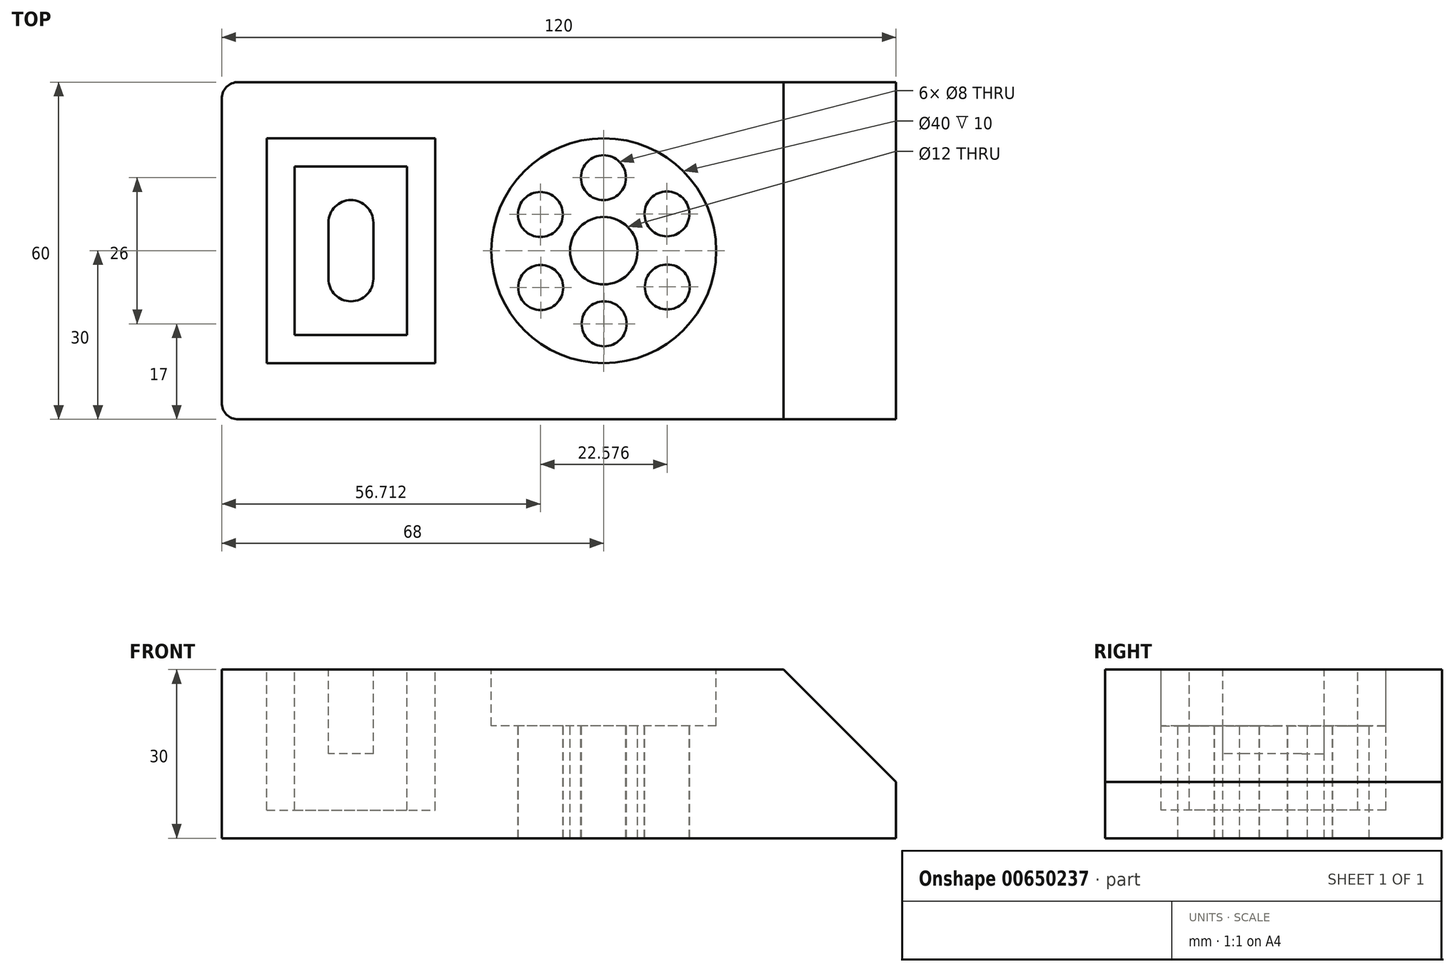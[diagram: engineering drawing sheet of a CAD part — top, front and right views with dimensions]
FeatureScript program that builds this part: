
annotation { "Feature Type Name" : "Feature", "Feature Type Description" : "" }
export const myFeature = defineFeature(function(context is Context, id is Id, definition is map)
    precondition{}
    {
        {
            var Q0;
            Q0=qCreatedBy(makeId("Front.planeOp"),FACE);
            var sketch = newSketch(context, id + "F0", { "sketchPlane" : qUnion([Q0])});
            skLineSegment(sketch, "E0", {"start": v(0, 0) * mm, "end": v(0, 50) * mm});
            skLineSegment(sketch, "E1", {"start": v(0, 50) * mm, "end": v(-120, 50) * mm});
            skLineSegment(sketch, "E2", {"start": v(-120, 50) * mm, "end": v(-120, 0) * mm});
            skLineSegment(sketch, "E3", {"start": v(-120, 0) * mm, "end": v(0, 0) * mm});
            skSolve(sketch);
        }
        {
            var Q0;
            Q0=makeQuery(id+"F0.imprint","IMPRINT",FACE,{"disambiguationData":[TD([[makeQuery(id+"F0.imprint","IMPRINT",EDGE,{"derivedFrom":sQuery(id+"F0.wireOp",EDGE,"E0")}),1.0]])]});
            extrude(context, id + "F1", {"entities" : qUnion([Q0]), "depth" : 60 * mm, "offsetDistance" : 25 * mm});
        }
        {
            var Q0;
            Q0=makeQuery(id+"F1.opExtrude","SWEPT_FACE",FACE,{"disambiguationData":[OSD([sQuery(id+"F0.wireOp",EDGE,"E1")])]});
            var sketch = newSketch(context, id + "F2", { "sketchPlane" : qUnion([Q0])});
            skLineSegment(sketch, "E4.bottom", {"start": v(-112, -10) * mm, "end": v(-82, -10) * mm});
            skLineSegment(sketch, "E4.top", {"start": v(-112, -50) * mm, "end": v(-82, -50) * mm});
            skLineSegment(sketch, "E4.left", {"start": v(-112, -10) * mm, "end": v(-112, -50) * mm});
            skLineSegment(sketch, "E4.right", {"start": v(-82, -10) * mm, "end": v(-82, -50) * mm});
            skLineSegment(sketch, "E5.bottom", {"start": v(-107, -15) * mm, "end": v(-87, -15) * mm});
            skLineSegment(sketch, "E5.top", {"start": v(-107, -45) * mm, "end": v(-87, -45) * mm});
            skLineSegment(sketch, "E5.left", {"start": v(-107, -15) * mm, "end": v(-107, -45) * mm});
            skLineSegment(sketch, "E5.right", {"start": v(-87, -15) * mm, "end": v(-87, -45) * mm});
            skSolve(sketch);
        }
        {
            var Q0;
            Q0=makeQuery(id+"F2.imprint","IMPRINT",FACE,{"disambiguationData":[TD([[makeQuery(id+"F2.imprint","IMPRINT",EDGE,{"derivedFrom":sQuery(id+"F2.wireOp",EDGE,"E4.bottom")}),-1.0]])]});
            extrude(context, id + "F3", {"entities" : qUnion([Q0]), "operationType" : NewBodyOperationType.REMOVE, "oppositeDirection" : true, "depth" : 25 * mm, "offsetDistance" : 25 * mm});
        }
        {
            var Q0;
            Q0=makeQuery(id+"F3.boolean.opBoolean","SPLIT",FACE,{"disambiguationData":[TD([makeQuery(id+"F3.opExtrude","SWEPT_FACE",FACE,{"disambiguationData":[OSD([sQuery(id+"F2.wireOp",EDGE,"E5.bottom")])]})])],"derivedFrom":makeQuery(id+"F1.opExtrude","SWEPT_FACE",FACE,{"disambiguationData":[OSD([sQuery(id+"F0.wireOp",EDGE,"E1")])]})});
            var sketch = newSketch(context, id + "F4", { "sketchPlane" : qUnion([Q0])});
            skLineSegment(sketch, "E6.bottom", {"start": v(-97, -21) * mm, "end": v(-97, -21) * mm});
            skLineSegment(sketch, "E6.top", {"start": v(-97, -39) * mm, "end": v(-97, -39) * mm});
            skLineSegment(sketch, "E6.left", {"start": v(-101, -25) * mm, "end": v(-101, -35) * mm});
            skLineSegment(sketch, "E6.right", {"start": v(-93, -25) * mm, "end": v(-93, -35) * mm});
            skPoint(sketch, "E7.visualSharp", {"position": v(-101, -21) * mm});
            skArc(sketch, "E7.filletArc", {"start": v(-97, -21) * mm, "mid": v(-99.83, -22.17) * mm, "end": v(-101, -25) * mm});
            skPoint(sketch, "E8.visualSharp", {"position": v(-93, -21) * mm});
            skArc(sketch, "E8.filletArc", {"start": v(-93, -25) * mm, "mid": v(-94.17, -22.17) * mm, "end": v(-97, -21) * mm});
            skPoint(sketch, "E9.visualSharp", {"position": v(-101, -39) * mm});
            skArc(sketch, "E9.filletArc", {"start": v(-101, -35) * mm, "mid": v(-99.83, -37.83) * mm, "end": v(-97, -39) * mm});
            skPoint(sketch, "E10.visualSharp", {"position": v(-93, -39) * mm});
            skArc(sketch, "E10.filletArc", {"start": v(-97, -39) * mm, "mid": v(-94.17, -37.83) * mm, "end": v(-93, -35) * mm});
            skSolve(sketch);
        }
        {
            var Q0;
            Q0=makeQuery(id+"F4.imprint","IMPRINT",FACE,{"disambiguationData":[TD([[makeQuery(id+"F4.imprint","IMPRINT",EDGE,{"derivedFrom":sQuery(id+"F4.wireOp",EDGE,"E6.left")}),1.0]])]});
            extrude(context, id + "F5", {"entities" : qUnion([Q0]), "operationType" : NewBodyOperationType.REMOVE, "oppositeDirection" : true, "depth" : 15 * mm, "offsetDistance" : 25 * mm});
        }
        {
            var Q0;
            Q0=makeQuery(id+"F1.opExtrude","SWEPT_FACE",FACE,{"disambiguationData":[OSD([sQuery(id+"F0.wireOp",EDGE,"E3")])]});
            var sketch = newSketch(context, id + "F6", { "sketchPlane" : qUnion([Q0])});
            skLineSegment(sketch, "E11.bottom", {"start": v(-120, 60) * mm, "end": v(0, 60) * mm});
            skLineSegment(sketch, "E11.top", {"start": v(-120, 0) * mm, "end": v(0, 0) * mm});
            skLineSegment(sketch, "E11.left", {"start": v(-120, 60) * mm, "end": v(-120, 0) * mm});
            skLineSegment(sketch, "E11.right", {"start": v(0, 60) * mm, "end": v(0, 0) * mm});
            skSolve(sketch);
        }
        {
            var Q0;
            Q0=makeQuery(id+"F1.opExtrude","SWEPT_EDGE",EDGE,{"disambiguationData":[OSD([sQuery(id+"F0.wireOp",EDGE,"E0"),sQuery(id+"F0.wireOp",EDGE,"E1")])]});
            chamfer(context, id + "F7", {"entities" : qUnion([Q0]), "width" : 20 * mm, "tangentPropagation" : true});
        }
        {
            var Q0;
            {var subQ2=sQuery(id+"F0.wireOp",EDGE,"E1");var subQ3=sQuery(id+"F0.wireOp",EDGE,"E0");Q0=makeQuery(id+"F3.boolean.opBoolean","SPLIT",FACE,{"disambiguationData":[TD([makeQuery(id+"F1.opExtrude","SWEPT_FACE",FACE,{"disambiguationData":[OSD([subQ3])]})])],"derivedFrom":makeQuery(id+"F1.opExtrude","SWEPT_FACE",FACE,{"disambiguationData":[OSD([subQ2])]})});}
            var sketch = newSketch(context, id + "F8", { "sketchPlane" : qUnion([Q0])});
            skCircle(sketch, "E12", {"center": v(-52, -30) * mm, "radius": 20 * mm});
            skPoint(sketch, "E12.centerSnap0", {"position": v(-82, -30) * mm});
            skSolve(sketch);
        }
        {
            var Q0;
            Q0=makeQuery(id+"F8.imprint","IMPRINT",FACE,{"disambiguationData":[TD([[makeQuery(id+"F8.imprint","IMPRINT",EDGE,{"derivedFrom":sQuery(id+"F8.wireOp",EDGE,"E12")}),1.0]])]});
            extrude(context, id + "F9", {"entities" : qUnion([Q0]), "operationType" : NewBodyOperationType.REMOVE, "oppositeDirection" : true, "depth" : 10 * mm, "offsetDistance" : 25 * mm});
        }
        {
            var Q0;
            Q0=makeQuery(id+"F9.boolean.opBoolean","COPY",FACE,{"derivedFrom":makeQuery(id+"F9.opExtrude","CAP_FACE",FACE,{"disambiguationData":[OSD([sQuery(id+"F8.wireOp",EDGE,"E12")])],"isStart":false})});
            var sketch = newSketch(context, id + "F10", { "sketchPlane" : qUnion([Q0])});
            skCircle(sketch, "E13", {"center": v(-63.23, -36.55) * mm, "radius": 4 * mm});
            skCircle(sketch, "E14.1.0", {"center": v(-63.29, -23.55) * mm, "radius": 4 * mm});
            skCircle(sketch, "E14.2.0", {"center": v(-52.06, -17) * mm, "radius": 4 * mm});
            skCircle(sketch, "E14.3.0", {"center": v(-40.77, -23.45) * mm, "radius": 4 * mm});
            skCircle(sketch, "E14.4.0", {"center": v(-40.71, -36.45) * mm, "radius": 4 * mm});
            skCircle(sketch, "E14.5.0", {"center": v(-51.94, -43) * mm, "radius": 4 * mm});
            skPoint(sketch, "E14.center", {"position": v(-52, -30) * mm});
            skLineSegment(sketch, "E14.anchor1", {"start": v(-52, -30) * mm, "end": v(-63.23, -36.55) * mm, "construction": true});
            skLineSegment(sketch, "E14.anchor2", {"start": v(-52, -30) * mm, "end": v(-51.94, -43) * mm, "construction": true});
            skSolve(sketch);
        }
        {
            var Q0;
            Q0=makeQuery(id+"F10.imprint","IMPRINT",FACE,{"disambiguationData":[TD([[makeQuery(id+"F10.imprint","IMPRINT",EDGE,{"derivedFrom":sQuery(id+"F10.wireOp",EDGE,"E14.2.0")}),1.0]])]});
            var Q1;
            Q1=makeQuery(id+"F10.imprint","IMPRINT",FACE,{"disambiguationData":[TD([[makeQuery(id+"F10.imprint","IMPRINT",EDGE,{"derivedFrom":sQuery(id+"F10.wireOp",EDGE,"E14.1.0")}),1.0]])]});
            var Q2;
            Q2=makeQuery(id+"F10.imprint","IMPRINT",FACE,{"disambiguationData":[TD([[makeQuery(id+"F10.imprint","IMPRINT",EDGE,{"derivedFrom":sQuery(id+"F10.wireOp",EDGE,"E13")}),1.0]])]});
            var Q3;
            Q3=makeQuery(id+"F10.imprint","IMPRINT",FACE,{"disambiguationData":[TD([[makeQuery(id+"F10.imprint","IMPRINT",EDGE,{"derivedFrom":sQuery(id+"F10.wireOp",EDGE,"E14.5.0")}),1.0]])]});
            var Q4;
            Q4=makeQuery(id+"F10.imprint","IMPRINT",FACE,{"disambiguationData":[TD([[makeQuery(id+"F10.imprint","IMPRINT",EDGE,{"derivedFrom":sQuery(id+"F10.wireOp",EDGE,"E14.4.0")}),1.0]])]});
            var Q5;
            Q5=makeQuery(id+"F10.imprint","IMPRINT",FACE,{"disambiguationData":[TD([[makeQuery(id+"F10.imprint","IMPRINT",EDGE,{"derivedFrom":sQuery(id+"F10.wireOp",EDGE,"E14.3.0")}),1.0]])]});
            extrude(context, id + "F11", {"entities" : qUnion([Q0, Q1, Q2, Q3, Q4, Q5]), "operationType" : NewBodyOperationType.REMOVE, "oppositeDirection" : true, "depth" : 20 * mm, "offsetDistance" : 25 * mm});
        }
        {
            var Q0;
            Q0 = qSketchRegion(id + "F6", true);
            extrude(context, id + "F12", {"entities" : qUnion([Q0]), "operationType" : NewBodyOperationType.REMOVE, "oppositeDirection" : true, "depth" : 20 * mm, "offsetDistance" : 25 * mm});
        }
        {
            var Q0;
            Q0=makeQuery(id+"F9.boolean.opBoolean","COPY",FACE,{"derivedFrom":makeQuery(id+"F9.opExtrude","CAP_FACE",FACE,{"disambiguationData":[OSD([sQuery(id+"F8.wireOp",EDGE,"E12")])],"isStart":false})});
            var sketch = newSketch(context, id + "F13", { "sketchPlane" : qUnion([Q0])});
            skCircle(sketch, "E15", {"center": v(-52, -30) * mm, "radius": 6 * mm});
            skSolve(sketch);
        }
        {
            var Q0;
            Q0=makeQuery(id+"F13.imprint","IMPRINT",FACE,{"disambiguationData":[TD([[makeQuery(id+"F13.imprint","IMPRINT",EDGE,{"derivedFrom":sQuery(id+"F13.wireOp",EDGE,"E15")}),1.0]])]});
            extrude(context, id + "F14", {"entities" : qUnion([Q0]), "operationType" : NewBodyOperationType.REMOVE, "oppositeDirection" : true, "depth" : 20 * mm, "offsetDistance" : 25 * mm});
        }
        {
            var Q0;
            Q0=makeQuery(id+"F1.opExtrude","CAP_EDGE",EDGE,{"disambiguationData":[OSD([sQuery(id+"F0.wireOp",EDGE,"E2")])],"isStart":false});
            fillet(context, id + "F15", {"entities" : qUnion([Q0]), "radius" : 3 * mm, "tangentPropagation" : true, "allowEdgeOverflow" : false});
        }
        {
            var Q0;
            Q0=makeQuery(id+"F1.opExtrude","CAP_EDGE",EDGE,{"disambiguationData":[OSD([sQuery(id+"F0.wireOp",EDGE,"E2")])],"isStart":true});
            fillet(context, id + "F16", {"entities" : qUnion([Q0]), "radius" : 3 * mm, "tangentPropagation" : true, "allowEdgeOverflow" : false});
        }
    });
